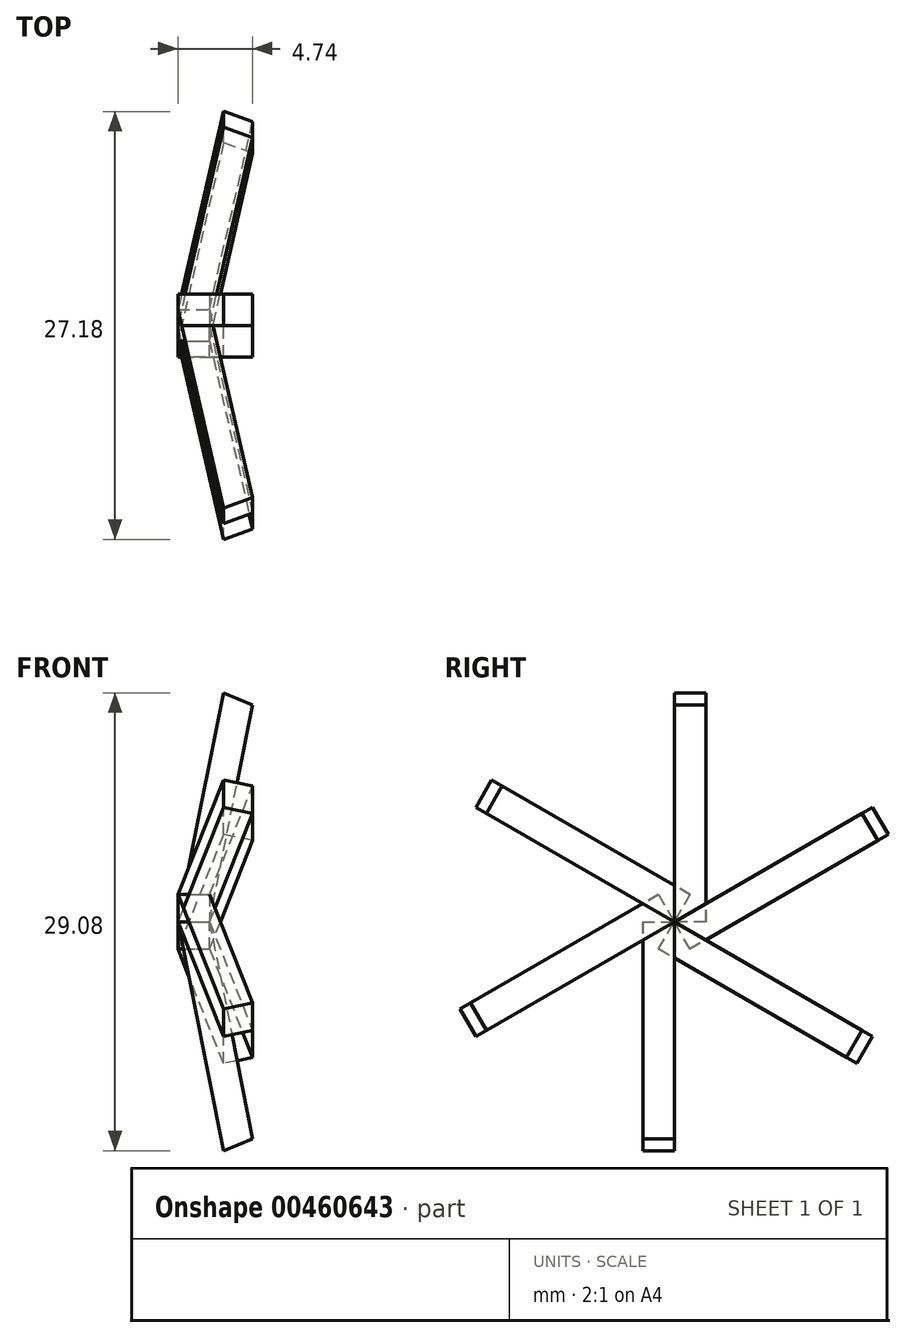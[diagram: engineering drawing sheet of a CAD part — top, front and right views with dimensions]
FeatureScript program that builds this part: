
annotation { "Feature Type Name" : "Feature", "Feature Type Description" : "" }
export const myFeature = defineFeature(function(context is Context, id is Id, definition is map)
    precondition{}
    {
        {
            var Q0;
            Q0=qCreatedBy(makeId("Front.planeOp"),FACE);
            var sketch = newSketch(context, id + "F0", { "sketchPlane" : qUnion([Q0])});
            skArc(sketch, "E0", {"start": v(0, 38) * mm, "mid": v(-38, 0) * mm, "end": v(0, -38) * mm, "construction": true});
            skLineSegment(sketch, "E1", {"start": v(0, 38) * mm, "end": v(0, -38) * mm, "construction": true});
            skLineSegment(sketch, "E2", {"start": v(0, 38) * mm, "end": v(0, 28.68) * mm});
            skLineSegment(sketch, "E3", {"start": v(0, -26.87) * mm, "end": v(-26.87, -26.87) * mm, "construction": true});
            skLineSegment(sketch, "E4", {"start": v(0, -14.54) * mm, "end": v(-35.1, -14.54) * mm, "construction": true});
            skLineSegment(sketch, "E5", {"start": v(0, -35.1) * mm, "end": v(-14.54, -35.1) * mm, "construction": true});
            skLineSegment(sketch, "E6", {"start": v(0, 0) * mm, "end": v(-14.54, 0) * mm});
            skLineSegment(sketch, "E7", {"start": v(0, -35.1) * mm, "end": v(0, -26.87) * mm});
            skLineSegment(sketch, "E8", {"start": v(0, -26.87) * mm, "end": v(0, -14.54) * mm});
            skLineSegment(sketch, "E9", {"start": v(0, -14.54) * mm, "end": v(0, 0) * mm});
            skLineSegment(sketch, "E10", {"start": v(0, -36.41) * mm, "end": v(0, -35.1) * mm});
            skPoint(sketch, "E11", {"position": v(-14.54, -35.1) * mm});
            skPoint(sketch, "E12", {"position": v(-26.87, -26.87) * mm});
            skPoint(sketch, "E13", {"position": v(-35.1, -14.54) * mm});
            skPoint(sketch, "E14", {"position": v(-38, 0) * mm});
            skPoint(sketch, "E15", {"position": v(0, -38) * mm});
            skLineSegment(sketch, "E16", {"start": v(0, 0) * mm, "end": v(-26.87, -26.87) * mm, "construction": true});
            skLineSegment(sketch, "E17", {"start": v(0, 0) * mm, "end": v(-35.1, -14.54) * mm, "construction": true});
            skLineSegment(sketch, "E18", {"start": v(0, 0) * mm, "end": v(-14.54, -35.1) * mm, "construction": true});
            skLineSegment(sketch, "E19", {"start": v(-35.1, -14.54) * mm, "end": v(-35.1, 0) * mm, "construction": true});
            skLineSegment(sketch, "E20", {"start": v(-35.1, -14.54) * mm, "end": v(-38, 0) * mm});
            skLineSegment(sketch, "E21", {"start": v(-36, 0) * mm, "end": v(-33.26, -13.78) * mm});
            skLineSegment(sketch, "E22", {"start": v(-33.26, -13.78) * mm, "end": v(-35.1, -14.54) * mm});
            skLineSegment(sketch, "E23", {"start": v(-38, 0) * mm, "end": v(-36, 0) * mm});
            skSolve(sketch);
        }
        {
            var Q0;
            Q0=qCreatedBy(makeId("Top.planeOp"),FACE);
            var sketch = newSketch(context, id + "F1", { "sketchPlane" : qUnion([Q0])});
            skCircle(sketch, "E24.cCircle", {"center": v(0, 0) * mm, "radius": 32.9 * mm, "construction": true});
            skLineSegment(sketch, "E24.0", {"start": v(19, -32.9) * mm, "end": v(-19, -32.9) * mm});
            skLineSegment(sketch, "E24.1", {"start": v(-19, -32.9) * mm, "end": v(-38, 0) * mm});
            skLineSegment(sketch, "E24.2", {"start": v(-38, 0) * mm, "end": v(-19, 32.9) * mm});
            skLineSegment(sketch, "E24.3", {"start": v(-19, 32.9) * mm, "end": v(19, 32.9) * mm});
            skLineSegment(sketch, "E24.4", {"start": v(19, 32.9) * mm, "end": v(38, 0) * mm});
            skLineSegment(sketch, "E24.5", {"start": v(38, 0) * mm, "end": v(19, -32.9) * mm});
            skPoint(sketch, "E24.0.midPoint", {"position": v(0, -32.9) * mm});
            skCircle(sketch, "E25", {"center": v(0, 0) * mm, "radius": 38 * mm});
            skLineSegment(sketch, "E26", {"start": v(0, 0) * mm, "end": v(-38, 0) * mm});
            skLineSegment(sketch, "E27", {"start": v(0, 0) * mm, "end": v(-35.1, 14.54) * mm});
            skLineSegment(sketch, "E28", {"start": v(0, 0) * mm, "end": v(-26.87, 26.87) * mm});
            skLineSegment(sketch, "E29", {"start": v(0, 0) * mm, "end": v(-14.54, 35.1) * mm});
            skLineSegment(sketch, "E30", {"start": v(0, 0) * mm, "end": v(0, 38) * mm});
            skSolve(sketch);
        }
        {
            var Q0;
            Q0=sQuery(id+"F0.wireOp",VERTEX,"E13");
            var Q1;
            Q1=sQuery(id+"F1.wireOp",VERTEX,"E27.end");
            var Q2;
            Q2=sQuery(id+"F0.wireOp",VERTEX,"E19.end");
            cPlane(context, id + "F2", {"entities" : qUnion([Q0, Q1, Q2]), "cplaneType" : CPlaneType.THREE_POINT, "offset" : 25 * mm, "width" : 150 * mm, "height" : 150 * mm});
        }
        {
            var Q0;
            Q0=qCreatedBy(id+"F2.planeOp",FACE);
            var sketch = newSketch(context, id + "F3", { "sketchPlane" : qUnion([Q0])});
            skCircle(sketch, "E31.cCircle", {"center": v(0, 0) * mm, "radius": 12.6 * mm, "construction": true});
            skLineSegment(sketch, "E31.0", {"start": v(-12.6, 7.27) * mm, "end": v(0, 14.54) * mm});
            skLineSegment(sketch, "E31.1", {"start": v(0, 14.54) * mm, "end": v(12.6, 7.27) * mm});
            skLineSegment(sketch, "E31.2", {"start": v(12.6, 7.27) * mm, "end": v(12.6, -7.27) * mm});
            skLineSegment(sketch, "E31.3", {"start": v(12.6, -7.27) * mm, "end": v(0, -14.54) * mm});
            skLineSegment(sketch, "E31.4", {"start": v(0, -14.54) * mm, "end": v(-12.6, -7.27) * mm});
            skLineSegment(sketch, "E31.5", {"start": v(-12.6, -7.27) * mm, "end": v(-12.6, 7.27) * mm});
            skPoint(sketch, "E31.0.midPoint", {"position": v(-6.3, 10.9) * mm});
            skSolve(sketch);
        }
        {
            var Q0;
            Q0=qSketchRegion(id+"F0",true);
            extrude(context, id + "F4", {"entities" : qUnion([Q0]), "depth" : 2 * mm, "offsetDistance" : 25 * mm});
        }
        {
            var Q0;
            Q0=sQuery(id+"F0.wireOp",VERTEX,"E13");
            var Q1;
            Q1=sQuery(id+"F0.wireOp",VERTEX,"E14");
            var Q2;
            Q2=sQuery(id+"F3.wireOp",VERTEX,"E31.3.start");
            cPlane(context, id + "F5", {"entities" : qUnion([Q0, Q1, Q2]), "cplaneType" : CPlaneType.THREE_POINT, "offset" : 25 * mm, "width" : 150 * mm, "height" : 150 * mm});
        }
        {
            var Q0;
            Q0=makeQuery(id+"F4.opExtrude","SWEPT_BODY",BODY,{"disambiguationData":[OSD([sQuery(id+"F0.wireOp",EDGE,"E20"),sQuery(id+"F0.wireOp",EDGE,"E21"),sQuery(id+"F0.wireOp",EDGE,"E22"),sQuery(id+"F0.wireOp",EDGE,"E23")])]});
            var Q1;
            Q1=sQuery(id+"F1.wireOp",EDGE,"E26");
            circularPattern(context, id + "F6", {"entities" : qUnion([Q0]), "axis" : qUnion([Q1]), "angle" : 360 * degree, "instanceCount" : 6, "equalSpace" : true});
        }
    });
